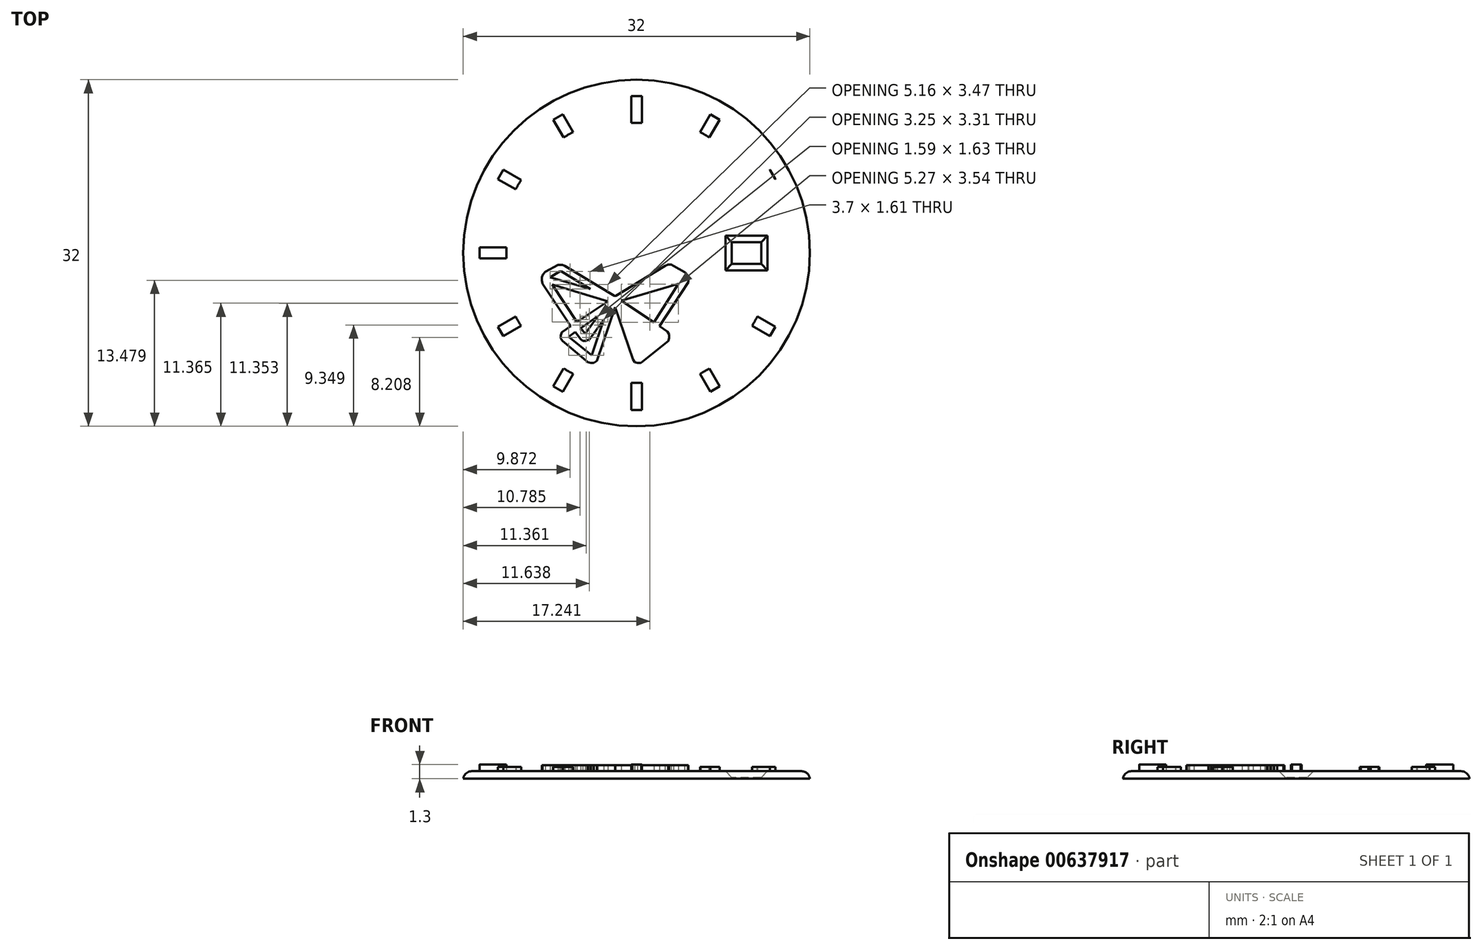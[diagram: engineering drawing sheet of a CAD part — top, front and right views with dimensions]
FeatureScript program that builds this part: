
annotation { "Feature Type Name" : "Feature", "Feature Type Description" : "" }
export const myFeature = defineFeature(function(context is Context, id is Id, definition is map)
    precondition{}
    {
        {
            var Q0;
            Q0=qCreatedBy(makeId("Top.planeOp"),FACE);
            var sketch = newSketch(context, id + "F0", { "sketchPlane" : qUnion([Q0])});
            skCircle(sketch, "E0", {"center": v(0, 0) * mm, "radius": 16 * mm});
            skLineSegment(sketch, "E1.bottom", {"start": v(8.8, 1) * mm, "end": v(11.5, 1) * mm});
            skLineSegment(sketch, "E1.top", {"start": v(8.8, -1) * mm, "end": v(11.5, -1) * mm});
            skLineSegment(sketch, "E1.left", {"start": v(8.8, 1) * mm, "end": v(8.8, -1) * mm});
            skLineSegment(sketch, "E1.right", {"start": v(11.5, 1) * mm, "end": v(11.5, -1) * mm});
            skLineSegment(sketch, "E2", {"start": v(-4.51, -9.01) * mm, "end": v(-7.42, -4.68) * mm});
            skLineSegment(sketch, "E3", {"start": v(-3.9, -8.61) * mm, "end": v(-0.72, -6.47) * mm});
            skLineSegment(sketch, "E4", {"start": v(-0.72, -6.47) * mm, "end": v(-6.45, -4.76) * mm});
            skLineSegment(sketch, "E5", {"start": v(-6.45, -4.76) * mm, "end": v(-3.9, -8.61) * mm});
            skLineSegment(sketch, "E6", {"start": v(-4.51, -9.01) * mm, "end": v(-5.44, -9.64) * mm});
            skLineSegment(sketch, "E7", {"start": v(-5.44, -9.64) * mm, "end": v(-5.54, -9.96) * mm});
            skLineSegment(sketch, "E8", {"start": v(-5.54, -9.96) * mm, "end": v(-5.54, -10.28) * mm});
            skLineSegment(sketch, "E9", {"start": v(-5.54, -10.28) * mm, "end": v(-5.38, -10.52) * mm});
            skLineSegment(sketch, "E10", {"start": v(-5.38, -10.52) * mm, "end": v(-2.76, -12.7) * mm});
            skLineSegment(sketch, "E11", {"start": v(-2.76, -12.7) * mm, "end": v(-2.48, -12.79) * mm});
            skLineSegment(sketch, "E12", {"start": v(-2.48, -12.79) * mm, "end": v(-2.15, -12.79) * mm});
            skLineSegment(sketch, "E13", {"start": v(-2.15, -12.79) * mm, "end": v(-1.84, -12.58) * mm});
            skLineSegment(sketch, "E14", {"start": v(-1.84, -12.58) * mm, "end": v(0.02, -7.06) * mm});
            skLineSegment(sketch, "E15", {"start": v(0.02, -7.06) * mm, "end": v(1.87, -12.45) * mm});
            skLineSegment(sketch, "E16", {"start": v(2.04, -12.7) * mm, "end": v(2.32, -12.79) * mm});
            skLineSegment(sketch, "E17", {"start": v(2.32, -12.79) * mm, "end": v(2.68, -12.79) * mm});
            skLineSegment(sketch, "E18", {"start": v(2.68, -12.79) * mm, "end": v(5.48, -10.52) * mm});
            skLineSegment(sketch, "E19", {"start": v(5.48, -10.52) * mm, "end": v(5.57, -10.22) * mm});
            skLineSegment(sketch, "E20", {"start": v(5.57, -10.22) * mm, "end": v(5.57, -9.85) * mm});
            skLineSegment(sketch, "E21", {"start": v(5.57, -9.85) * mm, "end": v(5.4, -9.58) * mm});
            skLineSegment(sketch, "E22", {"start": v(5.4, -9.58) * mm, "end": v(4.59, -9.01) * mm});
            skLineSegment(sketch, "E23", {"start": v(4.59, -9.01) * mm, "end": v(7.53, -4.5) * mm});
            skLineSegment(sketch, "E24", {"start": v(7.53, -4.5) * mm, "end": v(7.53, -4.14) * mm});
            skLineSegment(sketch, "E25", {"start": v(7.53, -4.14) * mm, "end": v(7.4, -3.8) * mm});
            skLineSegment(sketch, "E26", {"start": v(7.4, -3.8) * mm, "end": v(7.17, -3.47) * mm});
            skLineSegment(sketch, "E27", {"start": v(7.17, -3.47) * mm, "end": v(6.04, -2.83) * mm});
            skLineSegment(sketch, "E28", {"start": v(6.04, -2.83) * mm, "end": v(5.8, -2.7) * mm});
            skLineSegment(sketch, "E29", {"start": v(5.8, -2.7) * mm, "end": v(5.47, -2.7) * mm});
            skLineSegment(sketch, "E30", {"start": v(5.47, -2.7) * mm, "end": v(5.14, -2.84) * mm});
            skLineSegment(sketch, "E31", {"start": v(5.14, -2.84) * mm, "end": v(0.1, -5.92) * mm});
            skLineSegment(sketch, "E32", {"start": v(0.1, -5.92) * mm, "end": v(-0.04, -5.92) * mm});
            skLineSegment(sketch, "E33", {"start": v(-0.04, -5.92) * mm, "end": v(-5.14, -2.83) * mm});
            skLineSegment(sketch, "E34", {"start": v(-5.14, -2.83) * mm, "end": v(-5.37, -2.73) * mm});
            skLineSegment(sketch, "E35", {"start": v(-5.82, -2.73) * mm, "end": v(-7.14, -3.45) * mm});
            skLineSegment(sketch, "E36", {"start": v(-7.14, -3.45) * mm, "end": v(-7.4, -3.73) * mm});
            skLineSegment(sketch, "E37", {"start": v(-7.4, -3.73) * mm, "end": v(-7.5, -4) * mm});
            skLineSegment(sketch, "E38", {"start": v(-7.5, -4) * mm, "end": v(-7.5, -4.33) * mm});
            skLineSegment(sketch, "E39", {"start": v(-7.5, -4.33) * mm, "end": v(-7.42, -4.68) * mm});
            skLineSegment(sketch, "E40", {"start": v(-2.53, -5.2) * mm, "end": v(-6.64, -4) * mm});
            skLineSegment(sketch, "E41", {"start": v(-6.64, -4) * mm, "end": v(-5.65, -3.42) * mm});
            skLineSegment(sketch, "E42", {"start": v(-5.65, -3.42) * mm, "end": v(-5.47, -3.42) * mm});
            skLineSegment(sketch, "E43", {"start": v(-5.47, -3.42) * mm, "end": v(-2.53, -5.2) * mm});
            skLineSegment(sketch, "E44", {"start": v(0.76, -6.46) * mm, "end": v(6.62, -4.75) * mm});
            skLineSegment(sketch, "E45", {"start": v(6.62, -4.75) * mm, "end": v(4.1, -8.68) * mm});
            skLineSegment(sketch, "E46", {"start": v(4.1, -8.68) * mm, "end": v(0.76, -6.46) * mm});
            skLineSegment(sketch, "E47", {"start": v(-1.74, -7.99) * mm, "end": v(-3.04, -9.8) * mm});
            skLineSegment(sketch, "E48", {"start": v(-3.04, -9.8) * mm, "end": v(-3.52, -9.22) * mm});
            skLineSegment(sketch, "E49", {"start": v(-3.52, -9.22) * mm, "end": v(-1.74, -7.99) * mm});
            skLineSegment(sketch, "E50", {"start": v(-1.12, -8.33) * mm, "end": v(-2.36, -12) * mm});
            skLineSegment(sketch, "E51", {"start": v(-2.36, -12) * mm, "end": v(-4.74, -10.12) * mm});
            skLineSegment(sketch, "E52", {"start": v(-4.74, -10.12) * mm, "end": v(-4.07, -9.61) * mm});
            skLineSegment(sketch, "E53", {"start": v(-4.07, -9.61) * mm, "end": v(-3.5, -10.36) * mm});
            skLineSegment(sketch, "E54", {"start": v(-3.5, -10.36) * mm, "end": v(-3.27, -10.54) * mm});
            skLineSegment(sketch, "E55", {"start": v(-3.27, -10.54) * mm, "end": v(-2.97, -10.54) * mm});
            skLineSegment(sketch, "E56", {"start": v(-2.97, -10.54) * mm, "end": v(-2.59, -10.36) * mm});
            skLineSegment(sketch, "E57", {"start": v(-2.59, -10.36) * mm, "end": v(-1.12, -8.33) * mm});
            skLineSegment(sketch, "E58", {"start": v(-5.82, -2.73) * mm, "end": v(-5.37, -2.73) * mm});
            skLineSegment(sketch, "E59", {"start": v(0, 0) * mm, "end": v(0, 16) * mm});
            skText(sketch, "E60", { "text": "BERLIN", "fontName": "OpenSans-Bold.ttf"});
            const initialGuessF0  = {"E60": [-0.01023, 0.00388, 1, 0, 0.00412]};
            skSetInitialGuess(sketch, initialGuessF0);
            skSolve(sketch);
        }
        {
            var Q0;
            Q0=makeQuery(id+"F0.imprint","IMPRINT",FACE,{"disambiguationData":[TD([[makeQuery(id+"F0.imprint","IMPRINT",EDGE,{"derivedFrom":sQuery(id+"F0.wireOp",EDGE,"E0")}),1.0]])]});
            var Q1;
            Q1=makeQuery(id+"F0.imprint","IMPRINT",FACE,{"disambiguationData":[TD([[makeQuery(id+"F0.imprint","IMPRINT",EDGE,{"derivedFrom":sQuery(id+"F0.wireOp",EDGE,"E60.sketch_text.stroke-66")}),-1.0]])]});
            var Q2;
            Q2=makeQuery(id+"F0.imprint","IMPRINT",FACE,{"disambiguationData":[TD([[makeQuery(id+"F0.imprint","IMPRINT",EDGE,{"derivedFrom":sQuery(id+"F0.wireOp",EDGE,"E50")}),-1.0]])]});
            var Q3;
            Q3=makeQuery(id+"F0.imprint","IMPRINT",FACE,{"disambiguationData":[TD([[makeQuery(id+"F0.imprint","IMPRINT",EDGE,{"derivedFrom":sQuery(id+"F0.wireOp",EDGE,"E60.sketch_text.stroke-0")}),-1.0]])]});
            var Q4;
            Q4=makeQuery(id+"F0.imprint","IMPRINT",FACE,{"disambiguationData":[TD([[makeQuery(id+"F0.imprint","IMPRINT",EDGE,{"derivedFrom":sQuery(id+"F0.wireOp",EDGE,"E3")}),1.0]])]});
            var Q5;
            Q5=makeQuery(id+"F0.imprint","IMPRINT",FACE,{"disambiguationData":[TD([[makeQuery(id+"F0.imprint","IMPRINT",EDGE,{"derivedFrom":sQuery(id+"F0.wireOp",EDGE,"E40")}),-1.0]])]});
            var Q6;
            Q6=makeQuery(id+"F0.imprint","IMPRINT",FACE,{"disambiguationData":[TD([[makeQuery(id+"F0.imprint","IMPRINT",EDGE,{"derivedFrom":sQuery(id+"F0.wireOp",EDGE,"E60.sketch_text.stroke-12")}),1.0]])]});
            var Q7;
            {var subQ5=sQuery(id+"F0.wireOp",EDGE,"E60.sketch_text.stroke-51");Q7=makeQuery(id+"F0.imprint","IMPRINT",FACE,{"disambiguationData":[TD([[makeQuery(id+"F0.imprint","IMPRINT",EDGE,{"derivedFrom":subQ5}),1.0]])]});}
            var Q8;
            Q8=makeQuery(id+"F0.imprint","IMPRINT",FACE,{"disambiguationData":[TD([[makeQuery(id+"F0.imprint","IMPRINT",EDGE,{"derivedFrom":sQuery(id+"F0.wireOp",EDGE,"E60.sketch_text.stroke-56")}),-1.0]])]});
            var Q9;
            Q9=makeQuery(id+"F0.imprint","IMPRINT",FACE,{"disambiguationData":[TD([[makeQuery(id+"F0.imprint","IMPRINT",EDGE,{"derivedFrom":sQuery(id+"F0.wireOp",EDGE,"E60.sketch_text.stroke-62")}),-1.0]])]});
            var Q10;
            Q10=makeQuery(id+"F0.imprint","IMPRINT",FACE,{"disambiguationData":[TD([[makeQuery(id+"F0.imprint","IMPRINT",EDGE,{"derivedFrom":sQuery(id+"F0.wireOp",EDGE,"E60.sketch_text.stroke-25")}),-1.0]])]});
            var Q11;
            Q11=makeQuery(id+"F0.imprint","IMPRINT",FACE,{"disambiguationData":[TD([[makeQuery(id+"F0.imprint","IMPRINT",EDGE,{"derivedFrom":sQuery(id+"F0.wireOp",EDGE,"E60.sketch_text.stroke-37")}),-1.0]])]});
            var Q12;
            Q12=makeQuery(id+"F0.imprint","IMPRINT",FACE,{"disambiguationData":[TD([[makeQuery(id+"F0.imprint","IMPRINT",EDGE,{"derivedFrom":sQuery(id+"F0.wireOp",EDGE,"E60.sketch_text.stroke-19")}),1.0]])]});
            var Q13;
            Q13=makeQuery(id+"F0.imprint","IMPRINT",FACE,{"disambiguationData":[TD([[makeQuery(id+"F0.imprint","IMPRINT",EDGE,{"derivedFrom":sQuery(id+"F0.wireOp",EDGE,"E60.sketch_text.stroke-37")}),1.0]])]});
            var Q14;
            Q14=makeQuery(id+"F0.imprint","IMPRINT",FACE,{"disambiguationData":[TD([[makeQuery(id+"F0.imprint","IMPRINT",EDGE,{"derivedFrom":sQuery(id+"F0.wireOp",EDGE,"E44")}),-1.0]])]});
            var Q15;
            Q15=makeQuery(id+"F0.imprint","IMPRINT",FACE,{"disambiguationData":[TD([[makeQuery(id+"F0.imprint","IMPRINT",EDGE,{"derivedFrom":sQuery(id+"F0.wireOp",EDGE,"E47")}),-1.0]])]});
            var Q16;
            {var subQ0=sQuery(id+"F0.wireOp",EDGE,"E60.sketch_text.stroke-49");var subQ1=sQuery(id+"F0.wireOp",EDGE,"E59");var subQ2=makeQuery(id+"F0.imprint","INTERSECT",VERTEX,{"derivedFrom":[subQ1,subQ0]});Q16=makeQuery(id+"F0.imprint","IMPRINT",FACE,{"disambiguationData":[TD([[makeQuery(id+"F0.imprint","IMPRINT",EDGE,{"disambiguationData":[TD([[subQ2,1.0]])],"derivedFrom":subQ1}),-1.0]])]});}
            var Q17;
            {var subQ0=sQuery(id+"F0.wireOp",EDGE,"E60.sketch_text.stroke-53");var subQ1=sQuery(id+"F0.wireOp",EDGE,"E59");var subQ2=makeQuery(id+"F0.imprint","INTERSECT",VERTEX,{"derivedFrom":[subQ1,subQ0]});Q17=makeQuery(id+"F0.imprint","IMPRINT",FACE,{"disambiguationData":[TD([[makeQuery(id+"F0.imprint","IMPRINT",EDGE,{"disambiguationData":[TD([[subQ2,-1.0]])],"derivedFrom":subQ1}),-1.0]])]});}
            extrude(context, id + "F1", {"entities" : qUnion([Q0, Q1, Q2, Q3, Q4, Q5, Q6, Q7, Q8, Q9, Q10, Q11, Q12, Q13, Q14, Q15, Q16, Q17]), "oppositeDirection" : true, "depth" : .7 * mm, "offsetDistance" : 25 * mm});
        }
        {
            var Q0;
            Q0=qCreatedBy(makeId("Top.planeOp"),FACE);
            var sketch = newSketch(context, id + "F2", { "sketchPlane" : qUnion([Q0])});
            skLineSegment(sketch, "E61", {"start": v(-6.74, -7.5) * mm, "end": v(-9.65, -3.17) * mm});
            skLineSegment(sketch, "E62", {"start": v(-6.1, -7.1) * mm, "end": v(-2.93, -4.95) * mm});
            skLineSegment(sketch, "E63", {"start": v(-2.93, -4.95) * mm, "end": v(-8.66, -3.24) * mm});
            skLineSegment(sketch, "E64", {"start": v(-8.66, -3.24) * mm, "end": v(-6.1, -7.1) * mm});
            skLineSegment(sketch, "E65", {"start": v(-6.74, -7.5) * mm, "end": v(-7.67, -8.13) * mm});
            skLineSegment(sketch, "E66", {"start": v(-7.67, -8.13) * mm, "end": v(-7.76, -8.45) * mm});
            skLineSegment(sketch, "E67", {"start": v(-7.76, -8.45) * mm, "end": v(-7.76, -8.78) * mm});
            skLineSegment(sketch, "E68", {"start": v(-7.76, -8.78) * mm, "end": v(-7.6, -9) * mm});
            skLineSegment(sketch, "E69", {"start": v(-7.6, -9) * mm, "end": v(-4.99, -11.2) * mm});
            skLineSegment(sketch, "E70", {"start": v(-4.99, -11.2) * mm, "end": v(-4.7, -11.28) * mm});
            skLineSegment(sketch, "E71", {"start": v(-4.7, -11.28) * mm, "end": v(-4.37, -11.28) * mm});
            skLineSegment(sketch, "E72", {"start": v(-4.37, -11.28) * mm, "end": v(-4.06, -11.07) * mm});
            skLineSegment(sketch, "E73", {"start": v(-4.06, -11.07) * mm, "end": v(-2.2, -5.55) * mm});
            skLineSegment(sketch, "E74", {"start": v(-2.2, -5.55) * mm, "end": v(-0.36, -10.94) * mm});
            skLineSegment(sketch, "E75", {"start": v(-0.19, -11.2) * mm, "end": v(0.1, -11.28) * mm});
            skLineSegment(sketch, "E76", {"start": v(0.1, -11.28) * mm, "end": v(0.45, -11.28) * mm});
            skLineSegment(sketch, "E77", {"start": v(0.45, -11.28) * mm, "end": v(3.26, -9) * mm});
            skLineSegment(sketch, "E78", {"start": v(3.26, -9) * mm, "end": v(3.35, -8.71) * mm});
            skLineSegment(sketch, "E79", {"start": v(3.35, -8.71) * mm, "end": v(3.35, -8.34) * mm});
            skLineSegment(sketch, "E80", {"start": v(3.35, -8.34) * mm, "end": v(3.17, -8.07) * mm});
            skLineSegment(sketch, "E81", {"start": v(3.17, -8.07) * mm, "end": v(2.36, -7.5) * mm});
            skLineSegment(sketch, "E82", {"start": v(2.36, -7.5) * mm, "end": v(5.3, -3) * mm});
            skLineSegment(sketch, "E83", {"start": v(5.3, -3) * mm, "end": v(5.3, -2.63) * mm});
            skLineSegment(sketch, "E84", {"start": v(5.3, -2.63) * mm, "end": v(5.17, -2.29) * mm});
            skLineSegment(sketch, "E85", {"start": v(5.17, -2.29) * mm, "end": v(4.94, -1.96) * mm});
            skLineSegment(sketch, "E86", {"start": v(4.94, -1.96) * mm, "end": v(3.8, -1.32) * mm});
            skLineSegment(sketch, "E87", {"start": v(3.8, -1.32) * mm, "end": v(3.57, -1.2) * mm});
            skLineSegment(sketch, "E88", {"start": v(3.57, -1.2) * mm, "end": v(3.24, -1.2) * mm});
            skLineSegment(sketch, "E89", {"start": v(3.24, -1.2) * mm, "end": v(2.91, -1.33) * mm});
            skLineSegment(sketch, "E90", {"start": v(2.91, -1.33) * mm, "end": v(-2.12, -4.41) * mm});
            skLineSegment(sketch, "E91", {"start": v(-2.12, -4.41) * mm, "end": v(-2.27, -4.41) * mm});
            skLineSegment(sketch, "E92", {"start": v(-2.27, -4.41) * mm, "end": v(-7.37, -1.32) * mm});
            skLineSegment(sketch, "E93", {"start": v(-7.37, -1.32) * mm, "end": v(-7.6, -1.21) * mm});
            skLineSegment(sketch, "E94", {"start": v(-8.05, -1.21) * mm, "end": v(-9.37, -1.94) * mm});
            skLineSegment(sketch, "E95", {"start": v(-9.37, -1.94) * mm, "end": v(-9.62, -2.22) * mm});
            skLineSegment(sketch, "E96", {"start": v(-9.62, -2.22) * mm, "end": v(-9.73, -2.49) * mm});
            skLineSegment(sketch, "E97", {"start": v(-9.73, -2.49) * mm, "end": v(-9.73, -2.83) * mm});
            skLineSegment(sketch, "E98", {"start": v(-9.73, -2.83) * mm, "end": v(-9.65, -3.17) * mm});
            skLineSegment(sketch, "E99", {"start": v(-4.76, -3.7) * mm, "end": v(-8.86, -2.49) * mm});
            skLineSegment(sketch, "E100", {"start": v(-8.86, -2.49) * mm, "end": v(-7.87, -1.9) * mm});
            skLineSegment(sketch, "E101", {"start": v(-7.87, -1.9) * mm, "end": v(-7.7, -1.9) * mm});
            skLineSegment(sketch, "E102", {"start": v(-7.7, -1.9) * mm, "end": v(-4.76, -3.7) * mm});
            skLineSegment(sketch, "E103", {"start": v(-1.55, -4.9) * mm, "end": v(4.3, -3.18) * mm});
            skLineSegment(sketch, "E104", {"start": v(4.3, -3.18) * mm, "end": v(1.78, -7.12) * mm});
            skLineSegment(sketch, "E105", {"start": v(1.78, -7.12) * mm, "end": v(-1.55, -4.9) * mm});
            skLineSegment(sketch, "E106", {"start": v(-3.96, -6.49) * mm, "end": v(-5.26, -8.3) * mm});
            skLineSegment(sketch, "E107", {"start": v(-5.26, -8.3) * mm, "end": v(-5.73, -7.72) * mm});
            skLineSegment(sketch, "E108", {"start": v(-5.73, -7.72) * mm, "end": v(-3.96, -6.49) * mm});
            skLineSegment(sketch, "E109", {"start": v(-3.35, -6.82) * mm, "end": v(-4.58, -10.5) * mm});
            skLineSegment(sketch, "E110", {"start": v(-4.58, -10.5) * mm, "end": v(-6.96, -8.61) * mm});
            skLineSegment(sketch, "E111", {"start": v(-6.96, -8.61) * mm, "end": v(-6.3, -8.1) * mm});
            skLineSegment(sketch, "E112", {"start": v(-6.3, -8.1) * mm, "end": v(-5.73, -8.85) * mm});
            skLineSegment(sketch, "E113", {"start": v(-5.73, -8.85) * mm, "end": v(-5.5, -9.03) * mm});
            skLineSegment(sketch, "E114", {"start": v(-5.5, -9.03) * mm, "end": v(-5.2, -9.03) * mm});
            skLineSegment(sketch, "E115", {"start": v(-5.2, -9.03) * mm, "end": v(-4.81, -8.85) * mm});
            skLineSegment(sketch, "E116", {"start": v(-4.81, -8.85) * mm, "end": v(-3.35, -6.82) * mm});
            skLineSegment(sketch, "E117", {"start": v(-8.05, -1.21) * mm, "end": v(-7.6, -1.21) * mm});
            skLineSegment(sketch, "E118", {"start": v(-0.19, -11.2) * mm, "end": v(-0.36, -10.94) * mm});
            skSolve(sketch);
        }
        {
            var Q0;
            Q0=qSketchRegion(id+"F2",true);
            extrude(context, id + "F3", {"entities" : qUnion([Q0]), "depth" : 0.6 * mm, "offsetDistance" : 25 * mm});
        }
        {
            var Q0;
            Q0=makeQuery(id+"F1.opExtrude","CAP_EDGE",EDGE,{"disambiguationData":[OSD([sQuery(id+"F0.wireOp",EDGE,"E1.bottom")])],"isStart":true});
            var Q1;
            Q1=makeQuery(id+"F1.opExtrude","CAP_EDGE",EDGE,{"disambiguationData":[OSD([sQuery(id+"F0.wireOp",EDGE,"E1.left")])],"isStart":true});
            var Q2;
            Q2=makeQuery(id+"F1.opExtrude","CAP_EDGE",EDGE,{"disambiguationData":[OSD([sQuery(id+"F0.wireOp",EDGE,"E1.right")])],"isStart":true});
            var Q3;
            Q3=makeQuery(id+"F1.opExtrude","CAP_EDGE",EDGE,{"disambiguationData":[OSD([sQuery(id+"F0.wireOp",EDGE,"E1.top")])],"isStart":true});
            chamfer(context, id + "F4", {"entities" : qUnion([Q0, Q1, Q2, Q3]), "width" : 0.6 * mm, "tangentPropagation" : true});
        }
        {
            var Q0;
            Q0=makeQuery(id+"F1.opExtrude","CAP_EDGE",EDGE,{"disambiguationData":[OSD([sQuery(id+"F0.wireOp",EDGE,"E0")])],"isStart":true});
            fillet(context, id + "F5", {"entities" : qUnion([Q0]), "radius" : 0.8 * mm, "tangentPropagation" : true, "allowEdgeOverflow" : false});
        }
        {
            var Q0;
            Q0=qCreatedBy(makeId("Top.planeOp"),FACE);
            var sketch = newSketch(context, id + "F6", { "sketchPlane" : qUnion([Q0])});
            skCircle(sketch, "E119.0", {"center": v(0, 0) * mm, "radius": 12 * mm});
            skCircle(sketch, "E120.0", {"center": v(0, 0) * mm, "radius": 14.5 * mm});
            skLineSegment(sketch, "E121.0", {"start": v(-12, 0.5) * mm, "end": v(-14.5, 0.5) * mm});
            skLineSegment(sketch, "E122.0", {"start": v(-12, -0.5) * mm, "end": v(-14.5, -0.5) * mm});
            skLineSegment(sketch, "E123", {"start": v(-12, 0.5) * mm, "end": v(-12, -0.5) * mm});
            skLineSegment(sketch, "E124", {"start": v(-14.5, 0.5) * mm, "end": v(-14.5, -0.5) * mm});
            skLineSegment(sketch, "E125.0", {"start": v(0.5, 12) * mm, "end": v(0.5, 14.5) * mm});
            skLineSegment(sketch, "E126.0", {"start": v(-0.5, 12) * mm, "end": v(-0.5, 14.5) * mm});
            skLineSegment(sketch, "E127", {"start": v(-0.5, 14.5) * mm, "end": v(0.5, 14.5) * mm});
            skLineSegment(sketch, "E128", {"start": v(-0.5, 12) * mm, "end": v(0.5, 12) * mm});
            skLineSegment(sketch, "E129.0", {"start": v(0.5, -14.5) * mm, "end": v(0.5, -12) * mm});
            skLineSegment(sketch, "E130.0", {"start": v(-0.5, -14.5) * mm, "end": v(-0.5, -12) * mm});
            skLineSegment(sketch, "E131", {"start": v(-0.5, -12) * mm, "end": v(0.5, -12) * mm});
            skLineSegment(sketch, "E132", {"start": v(-0.5, -14.5) * mm, "end": v(0.5, -14.5) * mm});
            skCircle(sketch, "E133.0", {"center": v(0, 0) * mm, "radius": 12.6 * mm});
            skLineSegment(sketch, "E134.0", {"start": v(-5.87, -11.16) * mm, "end": v(-6.82, -12.8) * mm});
            skLineSegment(sketch, "E135.0", {"start": v(-6.73, -10.66) * mm, "end": v(-7.68, -12.3) * mm});
            skLineSegment(sketch, "E136.0", {"start": v(-11.16, -5.87) * mm, "end": v(-12.8, -6.82) * mm});
            skLineSegment(sketch, "E137.0", {"start": v(-10.66, -6.73) * mm, "end": v(-12.3, -7.68) * mm});
            skLineSegment(sketch, "E138", {"start": v(-12.3, -7.68) * mm, "end": v(-12.8, -6.82) * mm});
            skLineSegment(sketch, "E139", {"start": v(-11.16, -5.87) * mm, "end": v(-10.66, -6.73) * mm});
            skLineSegment(sketch, "E140", {"start": v(-7.68, -12.3) * mm, "end": v(-6.82, -12.8) * mm});
            skLineSegment(sketch, "E141", {"start": v(-6.73, -10.66) * mm, "end": v(-5.87, -11.16) * mm});
            skLineSegment(sketch, "E142", {"start": v(-6.82, -12.8) * mm, "end": v(-7.68, -12.3) * mm});
            skLineSegment(sketch, "E143.0", {"start": v(5.87, -11.16) * mm, "end": v(6.82, -12.8) * mm});
            skLineSegment(sketch, "E144.0", {"start": v(6.73, -10.66) * mm, "end": v(7.68, -12.3) * mm});
            skLineSegment(sketch, "E145.0", {"start": v(10.66, -6.73) * mm, "end": v(12.3, -7.68) * mm});
            skLineSegment(sketch, "E146.0", {"start": v(11.16, -5.87) * mm, "end": v(12.8, -6.82) * mm});
            skLineSegment(sketch, "E147.0", {"start": v(6.73, 10.66) * mm, "end": v(7.68, 12.3) * mm});
            skLineSegment(sketch, "E148.0", {"start": v(5.87, 11.16) * mm, "end": v(6.82, 12.8) * mm});
            skLineSegment(sketch, "E149.0", {"start": v(11.16, 5.87) * mm, "end": v(12.8, 6.82) * mm});
            skLineSegment(sketch, "E150.0", {"start": v(10.66, 6.73) * mm, "end": v(12.3, 7.68) * mm});
            skLineSegment(sketch, "E151.0", {"start": v(-5.87, 11.16) * mm, "end": v(-6.82, 12.8) * mm});
            skLineSegment(sketch, "E152.0", {"start": v(-6.73, 10.66) * mm, "end": v(-7.68, 12.3) * mm});
            skLineSegment(sketch, "E153.0", {"start": v(-10.66, 6.73) * mm, "end": v(-12.3, 7.68) * mm});
            skLineSegment(sketch, "E154.0", {"start": v(-11.16, 5.87) * mm, "end": v(-12.8, 6.82) * mm});
            skLineSegment(sketch, "E155", {"start": v(-12.8, 6.82) * mm, "end": v(-12.3, 7.68) * mm});
            skLineSegment(sketch, "E156", {"start": v(-11.16, 5.87) * mm, "end": v(-10.66, 6.73) * mm});
            skLineSegment(sketch, "E157", {"start": v(-7.68, 12.3) * mm, "end": v(-6.82, 12.8) * mm});
            skLineSegment(sketch, "E158", {"start": v(-6.73, 10.66) * mm, "end": v(-5.87, 11.16) * mm});
            skLineSegment(sketch, "E159", {"start": v(5.87, 11.16) * mm, "end": v(6.73, 10.66) * mm});
            skLineSegment(sketch, "E160", {"start": v(6.82, 12.8) * mm, "end": v(7.68, 12.3) * mm});
            skLineSegment(sketch, "E161", {"start": v(10.66, 6.73) * mm, "end": v(11.16, 5.87) * mm});
            skLineSegment(sketch, "E162", {"start": v(12.3, 7.68) * mm, "end": v(12.8, 6.82) * mm});
            skLineSegment(sketch, "E163", {"start": v(11.16, -5.87) * mm, "end": v(10.66, -6.73) * mm});
            skLineSegment(sketch, "E164", {"start": v(12.3, -7.68) * mm, "end": v(12.8, -6.82) * mm});
            skLineSegment(sketch, "E165", {"start": v(5.87, -11.16) * mm, "end": v(6.73, -10.66) * mm});
            skLineSegment(sketch, "E166", {"start": v(6.82, -12.8) * mm, "end": v(7.68, -12.3) * mm});
            skSolve(sketch);
        }
        {
            var Q0;
            {var subQ0=sQuery(id+"F6.wireOp",EDGE,"E162");var subQ1=sQuery(id+"F6.wireOp",EDGE,"E120.0");var subQ2=makeQuery(id+"F6.imprint","INTERSECT",VERTEX,{"derivedFrom":[subQ1,subQ0]});Q0=makeQuery(id+"F6.imprint","IMPRINT",FACE,{"disambiguationData":[TD([[makeQuery(id+"F6.imprint","IMPRINT",EDGE,{"disambiguationData":[TD([[subQ2,1.0]])],"derivedFrom":subQ1}),-1.0]])]});}
            var Q1;
            {var subQ0=sQuery(id+"F6.wireOp",EDGE,"E162");var subQ1=sQuery(id+"F6.wireOp",EDGE,"E120.0");var subQ2=makeQuery(id+"F6.imprint","INTERSECT",VERTEX,{"derivedFrom":[subQ1,subQ0]});Q1=makeQuery(id+"F6.imprint","IMPRINT",FACE,{"disambiguationData":[TD([[makeQuery(id+"F6.imprint","IMPRINT",EDGE,{"disambiguationData":[TD([[subQ2,-1.0]])],"derivedFrom":subQ1}),-1.0]])]});}
            var Q2;
            {var subQ0=sQuery(id+"F6.wireOp",EDGE,"E147.0");var subQ1=sQuery(id+"F6.wireOp",EDGE,"E120.0");var subQ2=makeQuery(id+"F6.imprint","INTERSECT",VERTEX,{"derivedFrom":[subQ1,subQ0]});Q2=makeQuery(id+"F6.imprint","IMPRINT",FACE,{"disambiguationData":[TD([[makeQuery(id+"F6.imprint","IMPRINT",EDGE,{"disambiguationData":[TD([[subQ2,-1.0]])],"derivedFrom":subQ1}),-1.0]])]});}
            var Q3;
            {var subQ0=sQuery(id+"F6.wireOp",EDGE,"E160");var subQ1=sQuery(id+"F6.wireOp",EDGE,"E120.0");var subQ2=makeQuery(id+"F6.imprint","INTERSECT",VERTEX,{"derivedFrom":[subQ1,subQ0]});Q3=makeQuery(id+"F6.imprint","IMPRINT",FACE,{"disambiguationData":[TD([[makeQuery(id+"F6.imprint","IMPRINT",EDGE,{"disambiguationData":[TD([[subQ2,-1.0]])],"derivedFrom":subQ1}),-1.0]])]});}
            var Q4;
            {var subQ0=sQuery(id+"F6.wireOp",EDGE,"E125.0");var subQ1=sQuery(id+"F6.wireOp",EDGE,"E120.0");var subQ2=makeQuery(id+"F6.imprint","INTERSECT",VERTEX,{"derivedFrom":[subQ1,subQ0]});Q4=makeQuery(id+"F6.imprint","IMPRINT",FACE,{"disambiguationData":[TD([[makeQuery(id+"F6.imprint","IMPRINT",EDGE,{"disambiguationData":[TD([[subQ2,-1.0]])],"derivedFrom":subQ1}),-1.0]])]});}
            var Q5;
            {var subQ0=sQuery(id+"F6.wireOp",EDGE,"E127");var subQ1=sQuery(id+"F6.wireOp",EDGE,"E120.0");var subQ2=makeQuery(id+"F6.imprint","INTERSECT",VERTEX,{"derivedFrom":[subQ1,subQ0]});Q5=makeQuery(id+"F6.imprint","IMPRINT",FACE,{"disambiguationData":[TD([[makeQuery(id+"F6.imprint","IMPRINT",EDGE,{"disambiguationData":[TD([[subQ2,-1.0]])],"derivedFrom":subQ1}),-1.0]])]});}
            var Q6;
            {var subQ0=sQuery(id+"F6.wireOp",EDGE,"E151.0");var subQ1=sQuery(id+"F6.wireOp",EDGE,"E120.0");var subQ2=makeQuery(id+"F6.imprint","INTERSECT",VERTEX,{"derivedFrom":[subQ1,subQ0]});Q6=makeQuery(id+"F6.imprint","IMPRINT",FACE,{"disambiguationData":[TD([[makeQuery(id+"F6.imprint","IMPRINT",EDGE,{"disambiguationData":[TD([[subQ2,-1.0]])],"derivedFrom":subQ1}),-1.0]])]});}
            var Q7;
            {var subQ0=sQuery(id+"F6.wireOp",EDGE,"E157");var subQ1=sQuery(id+"F6.wireOp",EDGE,"E120.0");var subQ2=makeQuery(id+"F6.imprint","INTERSECT",VERTEX,{"derivedFrom":[subQ1,subQ0]});Q7=makeQuery(id+"F6.imprint","IMPRINT",FACE,{"disambiguationData":[TD([[makeQuery(id+"F6.imprint","IMPRINT",EDGE,{"disambiguationData":[TD([[subQ2,-1.0]])],"derivedFrom":subQ1}),-1.0]])]});}
            var Q8;
            {var subQ0=sQuery(id+"F6.wireOp",EDGE,"E153.0");var subQ1=sQuery(id+"F6.wireOp",EDGE,"E120.0");var subQ2=makeQuery(id+"F6.imprint","INTERSECT",VERTEX,{"derivedFrom":[subQ1,subQ0]});Q8=makeQuery(id+"F6.imprint","IMPRINT",FACE,{"disambiguationData":[TD([[makeQuery(id+"F6.imprint","IMPRINT",EDGE,{"disambiguationData":[TD([[subQ2,-1.0]])],"derivedFrom":subQ1}),-1.0]])]});}
            var Q9;
            {var subQ0=sQuery(id+"F6.wireOp",EDGE,"E155");var subQ1=sQuery(id+"F6.wireOp",EDGE,"E120.0");var subQ2=makeQuery(id+"F6.imprint","INTERSECT",VERTEX,{"derivedFrom":[subQ1,subQ0]});Q9=makeQuery(id+"F6.imprint","IMPRINT",FACE,{"disambiguationData":[TD([[makeQuery(id+"F6.imprint","IMPRINT",EDGE,{"disambiguationData":[TD([[subQ2,-1.0]])],"derivedFrom":subQ1}),-1.0]])]});}
            var Q10;
            {var subQ0=sQuery(id+"F6.wireOp",EDGE,"E121.0");var subQ1=sQuery(id+"F6.wireOp",EDGE,"E120.0");var subQ2=makeQuery(id+"F6.imprint","INTERSECT",VERTEX,{"derivedFrom":[subQ1,subQ0]});Q10=makeQuery(id+"F6.imprint","IMPRINT",FACE,{"disambiguationData":[TD([[makeQuery(id+"F6.imprint","IMPRINT",EDGE,{"disambiguationData":[TD([[subQ2,-1.0]])],"derivedFrom":subQ1}),-1.0]])]});}
            var Q11;
            {var subQ0=sQuery(id+"F6.wireOp",EDGE,"E124");var subQ1=sQuery(id+"F6.wireOp",EDGE,"E120.0");var subQ2=makeQuery(id+"F6.imprint","INTERSECT",VERTEX,{"derivedFrom":[subQ1,subQ0]});Q11=makeQuery(id+"F6.imprint","IMPRINT",FACE,{"disambiguationData":[TD([[makeQuery(id+"F6.imprint","IMPRINT",EDGE,{"disambiguationData":[TD([[subQ2,-1.0]])],"derivedFrom":subQ1}),-1.0]])]});}
            var Q12;
            {var subQ0=sQuery(id+"F6.wireOp",EDGE,"E136.0");var subQ1=sQuery(id+"F6.wireOp",EDGE,"E120.0");var subQ2=makeQuery(id+"F6.imprint","INTERSECT",VERTEX,{"derivedFrom":[subQ1,subQ0]});Q12=makeQuery(id+"F6.imprint","IMPRINT",FACE,{"disambiguationData":[TD([[makeQuery(id+"F6.imprint","IMPRINT",EDGE,{"disambiguationData":[TD([[subQ2,-1.0]])],"derivedFrom":subQ1}),-1.0]])]});}
            var Q13;
            {var subQ0=sQuery(id+"F6.wireOp",EDGE,"E138");var subQ1=sQuery(id+"F6.wireOp",EDGE,"E120.0");var subQ2=makeQuery(id+"F6.imprint","INTERSECT",VERTEX,{"derivedFrom":[subQ1,subQ0]});Q13=makeQuery(id+"F6.imprint","IMPRINT",FACE,{"disambiguationData":[TD([[makeQuery(id+"F6.imprint","IMPRINT",EDGE,{"disambiguationData":[TD([[subQ2,-1.0]])],"derivedFrom":subQ1}),-1.0]])]});}
            var Q14;
            {var subQ0=sQuery(id+"F6.wireOp",EDGE,"E135.0");var subQ1=sQuery(id+"F6.wireOp",EDGE,"E120.0");var subQ2=makeQuery(id+"F6.imprint","INTERSECT",VERTEX,{"derivedFrom":[subQ1,subQ0]});Q14=makeQuery(id+"F6.imprint","IMPRINT",FACE,{"disambiguationData":[TD([[makeQuery(id+"F6.imprint","IMPRINT",EDGE,{"disambiguationData":[TD([[subQ2,-1.0]])],"derivedFrom":subQ1}),-1.0]])]});}
            var Q15;
            {var subQ0=sQuery(id+"F6.wireOp",EDGE,"E142");var subQ1=sQuery(id+"F6.wireOp",EDGE,"E120.0");var subQ2=makeQuery(id+"F6.imprint","INTERSECT",VERTEX,{"derivedFrom":[subQ1,subQ0]});Q15=makeQuery(id+"F6.imprint","IMPRINT",FACE,{"disambiguationData":[TD([[makeQuery(id+"F6.imprint","IMPRINT",EDGE,{"disambiguationData":[TD([[subQ2,-1.0]])],"derivedFrom":subQ1}),-1.0]])]});}
            var Q16;
            {var subQ0=sQuery(id+"F6.wireOp",EDGE,"E130.0");var subQ1=sQuery(id+"F6.wireOp",EDGE,"E120.0");var subQ2=makeQuery(id+"F6.imprint","INTERSECT",VERTEX,{"derivedFrom":[subQ1,subQ0]});Q16=makeQuery(id+"F6.imprint","IMPRINT",FACE,{"disambiguationData":[TD([[makeQuery(id+"F6.imprint","IMPRINT",EDGE,{"disambiguationData":[TD([[subQ2,-1.0]])],"derivedFrom":subQ1}),-1.0]])]});}
            var Q17;
            {var subQ0=sQuery(id+"F6.wireOp",EDGE,"E132");var subQ1=sQuery(id+"F6.wireOp",EDGE,"E120.0");var subQ2=makeQuery(id+"F6.imprint","INTERSECT",VERTEX,{"derivedFrom":[subQ1,subQ0]});Q17=makeQuery(id+"F6.imprint","IMPRINT",FACE,{"disambiguationData":[TD([[makeQuery(id+"F6.imprint","IMPRINT",EDGE,{"disambiguationData":[TD([[subQ2,-1.0]])],"derivedFrom":subQ1}),-1.0]])]});}
            var Q18;
            {var subQ0=sQuery(id+"F6.wireOp",EDGE,"E143.0");var subQ1=sQuery(id+"F6.wireOp",EDGE,"E120.0");var subQ2=makeQuery(id+"F6.imprint","INTERSECT",VERTEX,{"derivedFrom":[subQ1,subQ0]});Q18=makeQuery(id+"F6.imprint","IMPRINT",FACE,{"disambiguationData":[TD([[makeQuery(id+"F6.imprint","IMPRINT",EDGE,{"disambiguationData":[TD([[subQ2,-1.0]])],"derivedFrom":subQ1}),-1.0]])]});}
            var Q19;
            {var subQ0=sQuery(id+"F6.wireOp",EDGE,"E166");var subQ1=sQuery(id+"F6.wireOp",EDGE,"E120.0");var subQ2=makeQuery(id+"F6.imprint","INTERSECT",VERTEX,{"derivedFrom":[subQ1,subQ0]});Q19=makeQuery(id+"F6.imprint","IMPRINT",FACE,{"disambiguationData":[TD([[makeQuery(id+"F6.imprint","IMPRINT",EDGE,{"disambiguationData":[TD([[subQ2,-1.0]])],"derivedFrom":subQ1}),-1.0]])]});}
            var Q20;
            {var subQ0=sQuery(id+"F6.wireOp",EDGE,"E145.0");var subQ1=sQuery(id+"F6.wireOp",EDGE,"E120.0");var subQ2=makeQuery(id+"F6.imprint","INTERSECT",VERTEX,{"derivedFrom":[subQ1,subQ0]});Q20=makeQuery(id+"F6.imprint","IMPRINT",FACE,{"disambiguationData":[TD([[makeQuery(id+"F6.imprint","IMPRINT",EDGE,{"disambiguationData":[TD([[subQ2,-1.0]])],"derivedFrom":subQ1}),-1.0]])]});}
            var Q21;
            {var subQ0=sQuery(id+"F6.wireOp",EDGE,"E164");var subQ1=sQuery(id+"F6.wireOp",EDGE,"E120.0");var subQ2=makeQuery(id+"F6.imprint","INTERSECT",VERTEX,{"derivedFrom":[subQ1,subQ0]});Q21=makeQuery(id+"F6.imprint","IMPRINT",FACE,{"disambiguationData":[TD([[makeQuery(id+"F6.imprint","IMPRINT",EDGE,{"disambiguationData":[TD([[subQ2,-1.0]])],"derivedFrom":subQ1}),-1.0]])]});}
            var Q22;
            {var subQ3=sQuery(id+"F6.wireOp",EDGE,"E120.0");var subQ6=makeQuery(id+"F6.imprint","INTERSECT",VERTEX,{"derivedFrom":[subQ3,sQuery(id+"F6.wireOp",EDGE,"E162")]});Q22=makeQuery(id+"F6.imprint","IMPRINT",FACE,{"disambiguationData":[TD([[makeQuery(id+"F6.imprint","IMPRINT",EDGE,{"disambiguationData":[TD([[subQ6,1.0]])],"derivedFrom":subQ3}),1.0]])]});}
            var Q23;
            {var subQ1=sQuery(id+"F6.wireOp",EDGE,"E147.0");var subQ3=sQuery(id+"F6.wireOp",EDGE,"E120.0");var subQ4=makeQuery(id+"F6.imprint","INTERSECT",VERTEX,{"derivedFrom":[subQ3,subQ1]});Q23=makeQuery(id+"F6.imprint","IMPRINT",FACE,{"disambiguationData":[TD([[makeQuery(id+"F6.imprint","IMPRINT",EDGE,{"disambiguationData":[TD([[subQ4,-1.0]])],"derivedFrom":subQ3}),1.0]])]});}
            var Q24;
            {var subQ3=sQuery(id+"F6.wireOp",EDGE,"E120.0");var subQ6=sQuery(id+"F6.wireOp",EDGE,"E151.0");var subQ8=makeQuery(id+"F6.imprint","INTERSECT",VERTEX,{"derivedFrom":[subQ3,subQ6]});Q24=makeQuery(id+"F6.imprint","IMPRINT",FACE,{"disambiguationData":[TD([[makeQuery(id+"F6.imprint","IMPRINT",EDGE,{"disambiguationData":[TD([[subQ8,-1.0]])],"derivedFrom":subQ3}),1.0]])]});}
            var Q25;
            {var subQ3=sQuery(id+"F6.wireOp",EDGE,"E120.0");var subQ5=sQuery(id+"F6.wireOp",EDGE,"E153.0");var subQ7=makeQuery(id+"F6.imprint","INTERSECT",VERTEX,{"derivedFrom":[subQ3,subQ5]});Q25=makeQuery(id+"F6.imprint","IMPRINT",FACE,{"disambiguationData":[TD([[makeQuery(id+"F6.imprint","IMPRINT",EDGE,{"disambiguationData":[TD([[subQ7,-1.0]])],"derivedFrom":subQ3}),1.0]])]});}
            var Q26;
            {var subQ1=sQuery(id+"F6.wireOp",EDGE,"E136.0");var subQ3=sQuery(id+"F6.wireOp",EDGE,"E120.0");var subQ4=makeQuery(id+"F6.imprint","INTERSECT",VERTEX,{"derivedFrom":[subQ3,subQ1]});Q26=makeQuery(id+"F6.imprint","IMPRINT",FACE,{"disambiguationData":[TD([[makeQuery(id+"F6.imprint","IMPRINT",EDGE,{"disambiguationData":[TD([[subQ4,-1.0]])],"derivedFrom":subQ3}),1.0]])]});}
            var Q27;
            {var subQ1=sQuery(id+"F6.wireOp",EDGE,"E135.0");var subQ3=sQuery(id+"F6.wireOp",EDGE,"E120.0");var subQ4=makeQuery(id+"F6.imprint","INTERSECT",VERTEX,{"derivedFrom":[subQ3,subQ1]});Q27=makeQuery(id+"F6.imprint","IMPRINT",FACE,{"disambiguationData":[TD([[makeQuery(id+"F6.imprint","IMPRINT",EDGE,{"disambiguationData":[TD([[subQ4,-1.0]])],"derivedFrom":subQ3}),1.0]])]});}
            var Q28;
            {var subQ3=sQuery(id+"F6.wireOp",EDGE,"E120.0");var subQ5=sQuery(id+"F6.wireOp",EDGE,"E143.0");var subQ7=makeQuery(id+"F6.imprint","INTERSECT",VERTEX,{"derivedFrom":[subQ3,subQ5]});Q28=makeQuery(id+"F6.imprint","IMPRINT",FACE,{"disambiguationData":[TD([[makeQuery(id+"F6.imprint","IMPRINT",EDGE,{"disambiguationData":[TD([[subQ7,-1.0]])],"derivedFrom":subQ3}),1.0]])]});}
            var Q29;
            {var subQ3=sQuery(id+"F6.wireOp",EDGE,"E120.0");var subQ5=sQuery(id+"F6.wireOp",EDGE,"E145.0");var subQ7=makeQuery(id+"F6.imprint","INTERSECT",VERTEX,{"derivedFrom":[subQ3,subQ5]});Q29=makeQuery(id+"F6.imprint","IMPRINT",FACE,{"disambiguationData":[TD([[makeQuery(id+"F6.imprint","IMPRINT",EDGE,{"disambiguationData":[TD([[subQ7,-1.0]])],"derivedFrom":subQ3}),1.0]])]});}
            var Q30;
            {var subQ3=sQuery(id+"F6.wireOp",EDGE,"E120.0");var subQ5=sQuery(id+"F6.wireOp",EDGE,"E162");var subQ12=makeQuery(id+"F6.imprint","INTERSECT",VERTEX,{"disambiguationData":[OD(0.0)],"derivedFrom":[subQ3,subQ5]});Q30=makeQuery(id+"F6.imprint","IMPRINT",FACE,{"disambiguationData":[TD([[makeQuery(id+"F6.imprint","IMPRINT",EDGE,{"disambiguationData":[TD([[subQ12,1.0]])],"derivedFrom":subQ3}),1.0]])]});}
            extrude(context, id + "F7", {"entities" : qUnion([Q0, Q1, Q2, Q3, Q4, Q5, Q6, Q7, Q8, Q9, Q10, Q11, Q12, Q13, Q14, Q15, Q16, Q17, Q18, Q19, Q20, Q21, Q22, Q23, Q24, Q25, Q26, Q27, Q28, Q29, Q30]), "depth" : .4 * mm, "offsetDistance" : 25 * mm});
        }
        {
            var Q0;
            Q0=makeQuery(id+"F3.opExtrude","SWEPT_BODY",BODY,{"disambiguationData":[OSD([sQuery(id+"F2.wireOp",EDGE,"E61"),sQuery(id+"F2.wireOp",EDGE,"E62"),sQuery(id+"F2.wireOp",EDGE,"E63"),sQuery(id+"F2.wireOp",EDGE,"E64"),sQuery(id+"F2.wireOp",EDGE,"E65"),sQuery(id+"F2.wireOp",EDGE,"E66"),sQuery(id+"F2.wireOp",EDGE,"E67"),sQuery(id+"F2.wireOp",EDGE,"E68"),sQuery(id+"F2.wireOp",EDGE,"E69"),sQuery(id+"F2.wireOp",EDGE,"E70"),sQuery(id+"F2.wireOp",EDGE,"E71"),sQuery(id+"F2.wireOp",EDGE,"E72"),sQuery(id+"F2.wireOp",EDGE,"E73"),sQuery(id+"F2.wireOp",EDGE,"E74"),sQuery(id+"F2.wireOp",EDGE,"E75"),sQuery(id+"F2.wireOp",EDGE,"E76"),sQuery(id+"F2.wireOp",EDGE,"E77"),sQuery(id+"F2.wireOp",EDGE,"E78"),sQuery(id+"F2.wireOp",EDGE,"E79"),sQuery(id+"F2.wireOp",EDGE,"E80"),sQuery(id+"F2.wireOp",EDGE,"E81"),sQuery(id+"F2.wireOp",EDGE,"E82"),sQuery(id+"F2.wireOp",EDGE,"E83"),sQuery(id+"F2.wireOp",EDGE,"E84"),sQuery(id+"F2.wireOp",EDGE,"E85"),sQuery(id+"F2.wireOp",EDGE,"E86"),sQuery(id+"F2.wireOp",EDGE,"E87"),sQuery(id+"F2.wireOp",EDGE,"E88"),sQuery(id+"F2.wireOp",EDGE,"E89"),sQuery(id+"F2.wireOp",EDGE,"E90"),sQuery(id+"F2.wireOp",EDGE,"E91"),sQuery(id+"F2.wireOp",EDGE,"E92"),sQuery(id+"F2.wireOp",EDGE,"E93"),sQuery(id+"F2.wireOp",EDGE,"E94"),sQuery(id+"F2.wireOp",EDGE,"E95"),sQuery(id+"F2.wireOp",EDGE,"E96"),sQuery(id+"F2.wireOp",EDGE,"E97"),sQuery(id+"F2.wireOp",EDGE,"E98"),sQuery(id+"F2.wireOp",EDGE,"E99"),sQuery(id+"F2.wireOp",EDGE,"E100"),sQuery(id+"F2.wireOp",EDGE,"E101"),sQuery(id+"F2.wireOp",EDGE,"E102"),sQuery(id+"F2.wireOp",EDGE,"E103"),sQuery(id+"F2.wireOp",EDGE,"E104"),sQuery(id+"F2.wireOp",EDGE,"E105"),sQuery(id+"F2.wireOp",EDGE,"E106"),sQuery(id+"F2.wireOp",EDGE,"E107"),sQuery(id+"F2.wireOp",EDGE,"E108"),sQuery(id+"F2.wireOp",EDGE,"E109"),sQuery(id+"F2.wireOp",EDGE,"E110"),sQuery(id+"F2.wireOp",EDGE,"E111"),sQuery(id+"F2.wireOp",EDGE,"E112"),sQuery(id+"F2.wireOp",EDGE,"E113"),sQuery(id+"F2.wireOp",EDGE,"E114"),sQuery(id+"F2.wireOp",EDGE,"E115"),sQuery(id+"F2.wireOp",EDGE,"E116"),sQuery(id+"F2.wireOp",EDGE,"E117"),sQuery(id+"F2.wireOp",EDGE,"E118")])]});
            var Q1;
            Q1=qCreatedBy(makeId("Origin.pointOp"),VERTEX);
            var Q2;
            Q2=qCreatedBy(makeId("Origin.pointOp"),VERTEX);
            transform(context, id + "F8", {"entities" : qUnion([Q0]), "transformType" : TransformType.SCALE_UNIFORMLY, "scale" : .9, "scalePoint" : qUnion([Q2]), "makeCopy" : false});
        }
        {
            var Q0;
            {var subQ1=sQuery(id+"F6.wireOp",EDGE,"E120.0");var subQ7=sQuery(id+"F6.wireOp",EDGE,"E121.0");var subQ8=makeQuery(id+"F6.imprint","INTERSECT",VERTEX,{"derivedFrom":[subQ1,subQ7]});Q0=makeQuery(id+"F6.imprint","IMPRINT",FACE,{"disambiguationData":[TD([[makeQuery(id+"F6.imprint","IMPRINT",EDGE,{"disambiguationData":[TD([[subQ8,-1.0]])],"derivedFrom":subQ1}),1.0]])]});}
            var Q1;
            {var subQ0=sQuery(id+"F6.wireOp",EDGE,"E123");var subQ3=sQuery(id+"F6.wireOp",EDGE,"E119.0");var subQ4=makeQuery(id+"F6.imprint","INTERSECT",VERTEX,{"disambiguationData":[OD(0.0)],"derivedFrom":[subQ3,subQ0]});Q1=makeQuery(id+"F6.imprint","IMPRINT",FACE,{"disambiguationData":[TD([[makeQuery(id+"F6.imprint","IMPRINT",EDGE,{"disambiguationData":[TD([[subQ4,-1.0]])],"derivedFrom":subQ3}),-1.0]])]});}
            var Q2;
            {var subQ1=sQuery(id+"F6.wireOp",EDGE,"E120.0");var subQ8=sQuery(id+"F6.wireOp",EDGE,"E130.0");var subQ9=makeQuery(id+"F6.imprint","INTERSECT",VERTEX,{"derivedFrom":[subQ1,subQ8]});Q2=makeQuery(id+"F6.imprint","IMPRINT",FACE,{"disambiguationData":[TD([[makeQuery(id+"F6.imprint","IMPRINT",EDGE,{"disambiguationData":[TD([[subQ9,-1.0]])],"derivedFrom":subQ1}),1.0]])]});}
            var Q3;
            {var subQ0=sQuery(id+"F6.wireOp",EDGE,"E131");var subQ3=sQuery(id+"F6.wireOp",EDGE,"E119.0");var subQ4=makeQuery(id+"F6.imprint","INTERSECT",VERTEX,{"disambiguationData":[OD(0.0)],"derivedFrom":[subQ3,subQ0]});Q3=makeQuery(id+"F6.imprint","IMPRINT",FACE,{"disambiguationData":[TD([[makeQuery(id+"F6.imprint","IMPRINT",EDGE,{"disambiguationData":[TD([[subQ4,-1.0]])],"derivedFrom":subQ3}),-1.0]])]});}
            var Q4;
            {var subQ0=sQuery(id+"F6.wireOp",EDGE,"E125.0");var subQ1=sQuery(id+"F6.wireOp",EDGE,"E120.0");var subQ2=makeQuery(id+"F6.imprint","INTERSECT",VERTEX,{"derivedFrom":[subQ1,subQ0]});Q4=makeQuery(id+"F6.imprint","IMPRINT",FACE,{"disambiguationData":[TD([[makeQuery(id+"F6.imprint","IMPRINT",EDGE,{"disambiguationData":[TD([[subQ2,-1.0]])],"derivedFrom":subQ1}),1.0]])]});}
            var Q5;
            {var subQ0=sQuery(id+"F6.wireOp",EDGE,"E128");var subQ3=sQuery(id+"F6.wireOp",EDGE,"E119.0");var subQ4=makeQuery(id+"F6.imprint","INTERSECT",VERTEX,{"disambiguationData":[OD(0.0)],"derivedFrom":[subQ3,subQ0]});Q5=makeQuery(id+"F6.imprint","IMPRINT",FACE,{"disambiguationData":[TD([[makeQuery(id+"F6.imprint","IMPRINT",EDGE,{"disambiguationData":[TD([[subQ4,1.0]])],"derivedFrom":subQ3}),-1.0]])]});}
            extrude(context, id + "F9", {"entities" : qUnion([Q0, Q1, Q2, Q3, Q4, Q5]), "depth" : .6 * mm, "offsetDistance" : 25 * mm});
        }
    });
